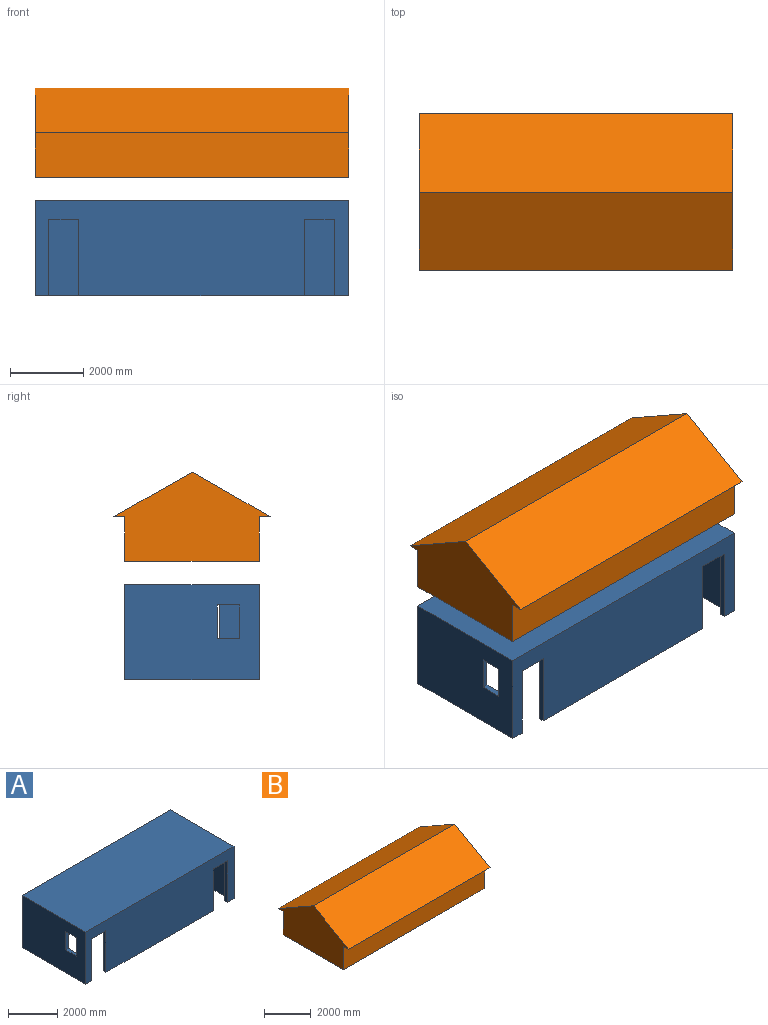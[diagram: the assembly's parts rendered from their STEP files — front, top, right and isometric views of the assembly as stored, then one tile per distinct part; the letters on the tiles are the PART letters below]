
ASSEMBLY  parts=2 mates=1
PART A: 25 faces, bbox 8534.4x3657.6x2590.8 mm
  f0: plane 1066.8x388.64mm, normal (0,0,-1), area 198582.7mm2, adj f3,f5,f6,f7,f12,f24
  f1: plane 3657.6x2590.8mm, normal (-1,0,0), area 8918519.2mm2, adj f3,f8,f9,f14,f18,f19,f20,f21
  f2: plane 3352.8x2438.4mm, normal (1,0,0), area 7617876.6mm2, adj f5,f9,f10,f13,f18,f19,f20,f21
  f3: plane 8534.4x2590.8mm, normal (0,-1,0), area 18741682.1mm2, adj f0,f1,f4,f7,f9,f14,f15,f16
  f4: plane 6160.99x152.4mm, normal (0,0,-1), area 938934.2mm2, adj f3,f5,f16,f23
  f5: plane 8229.6x2438.4mm, normal (0,1,0), area 16697815.2mm2, adj f0,f2,f4,f6,f9,f13,f15,f16
  f6: plane 3352.8x2438.4mm, normal (-1,0,0), area 2972897.3mm2, adj f0,f5,f10,f11,f12,f13
  f7: plane 3657.6x2590.8mm, normal (1,0,0), area 4273539.8mm2, adj f0,f3,f8,f9,f10,f11,f12,f14
  f8: plane 8534.4x2590.8mm, normal (0,1,0), area 22110923.5mm2, adj f1,f7,f9,f14
  f9: plane 8534.4x3657.6mm, normal (0,0,-1), area 1866351.2mm2, adj f1,f2,f3,f5,f7,f8,f10,f15
  f10: plane 8382x2438.4mm, normal (0,-1,0), area 20392217.3mm2, adj f2,f6,f7,f9,f11,f13
  f11: plane 2438.4x152.4mm, normal (0,0,-1), area 371612.2mm2, adj f6,f7,f10,f12
  f12: plane 2133.6x152.4mm, normal (0,1,0), area 325160.6mm2, adj f0,f6,f7,f11
  f13: plane 8229.6x3352.8mm, normal (0,0,-1), area 27592202.9mm2, adj f2,f5,f6,f10
  f14: plane 8534.4x3657.6mm, normal (0,0,1), area 31215421.4mm2, adj f1,f3,f7,f8
  f15: plane 2072.64x152.4mm, normal (1,0,0), area 315870.3mm2, adj f3,f5,f9,f17
  f16: plane 2072.64x152.4mm, normal (-1,0,0), area 315870.3mm2, adj f3,f4,f5,f17
  f17: plane 812.78x152.4mm, normal (0,0,-1), area 123867.6mm2, adj f3,f5,f15,f16
  f18: plane 615.87x152.4mm, normal (0,0,-1), area 93858mm2, adj f1,f2,f19,f21
  f19: plane 905.38x152.4mm, normal (0,-1,0), area 137979.4mm2, adj f1,f2,f18,f20
  f20: plane 615.87x152.4mm, normal (0,0,1), area 93858mm2, adj f1,f2,f19,f21
  f21: plane 905.38x152.4mm, normal (0,1,0), area 137979.4mm2, adj f1,f2,f18,f20
  f22: plane 812.8x152.4mm, normal (0,0,-1), area 123870.7mm2, adj f3,f5,f23,f24
  f23: plane 2072.64x152.4mm, normal (1,0,0), area 315870.3mm2, adj f3,f4,f5,f22
  f24: plane 2072.64x152.4mm, normal (-1,0,0), area 315870.3mm2, adj f0,f3,f5,f22
PART B: 14 faces, bbox 8534.4x4267.2x2438.4 mm
  f0: plane 8534.4x1219.2mm, normal (0,1,0), area 10405140.5mm2, adj f1,f7,f8,f11
  f1: plane 4267.2x2438.4mm, normal (-1,0,0), area 7060631mm2, adj f0,f2,f8,f9,f10,f11,f12
  f2: plane 8534.4x1219.2mm, normal (0,-1,0), area 10405140.5mm2, adj f1,f7,f8,f12
  f3: plane 3352.8x1219.2mm, normal (1,0,0), area 4087733.8mm2, adj f4,f6,f8,f13
  f4: plane 8229.6x1219.2mm, normal (0,-1,0), area 10033528.3mm2, adj f3,f5,f8,f13
  f5: plane 3352.8x1219.2mm, normal (-1,0,0), area 4087733.8mm2, adj f4,f6,f8,f13
  f6: plane 8229.6x1219.2mm, normal (0,1,0), area 10033528.3mm2, adj f3,f5,f8,f13
  f7: plane 4267.2x2438.4mm, normal (1,0,0), area 7060631mm2, adj f0,f2,f8,f9,f10,f11,f12
  f8: plane 8534.4x3657.6mm, normal (0,0,-1), area 3623218.6mm2, adj f0,f1,f2,f3,f4,f5,f6,f7
  f9: plane 8534.4x2123.12mm, normal (0,-0.5,0.87), area 20894596mm2, adj f1,f7,f10,f12
  f10: plane 8534.4x2144.08mm, normal (0,0.49,0.87), area 21049960.1mm2, adj f1,f7,f9,f11
  f11: plane 8534.4x304.8mm, normal (0,0,-1), area 2601285.1mm2, adj f0,f1,f7,f10
  f12: plane 8534.4x304.8mm, normal (0,0,-1), area 2601285.1mm2, adj f1,f2,f7,f9
  f13: plane 8229.6x3352.8mm, normal (0,0,-1), area 27592202.9mm2, adj f3,f4,f5,f6
PLACE A t=(264.46,-550.12,373.04)mm
PLACE B t=(3551.71,-500.29,3603.92)mm
MATE planar B.f7 <-> A.f7  axis (1,0,0) through (4781.21,-2318.61,3603.92)mm
